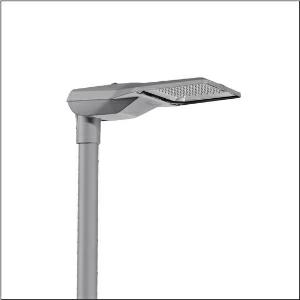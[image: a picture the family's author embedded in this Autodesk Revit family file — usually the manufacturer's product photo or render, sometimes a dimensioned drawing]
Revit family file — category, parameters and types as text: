
# Revit family: streetlight_sl_21_midi___st1_0a_5xe3d33s08nb_54c0
name_source: partatom
category: Lighting Fixtures
units: mm (PartAtom-declared; Revit-internal decimal feet)

## family parameters
Cut with Voids When Loaded = No
Host = Face
Light Source = No
Part Type = Normal
Room Calculation Point = No
Round Connector Dimension = Use Diameter
Shared = No

## types (1)
- --- (1 x LED, 22700 lm, 151.2 W, 3000K)
    Apparent Load = 151 VA
    CIE Flux Codes = 40 73 97 100 100
    Color Rendering = 70
    Color Temperature = 3000K
    Default Elevation = 1800 mm
    Description = Streetlight SL 21 midi, mast luminaire, primary light control with lens, of PMMA, primary optical cover: cover, of toughened safety glass, transparent, light distribution: ST1.0a, light emission: direct distribution, primary light characteristic: asymmetric, installation type: side-entry, post-top, LED, High Power LED, rated luminous flux: 22.700lm, luminous efficacy: 150lm/W, light colour: 730, colour temperature: 3000K, control: flexible luminous flux parameterisation, time-dependent luminous flux control, constant luminous flux control, overheat protection, presetting dimming logarithmic, mains connection: 230..240V, AC, 50/60Hz, start of lifetime: 151W, end of service life: 157W, reduction: 70W, luminaire housing, of diecast aluminium, powder-coated, Siteco® metallic grey (DB 702S), corrosivity category C5 mid according to DIN EN ISO 12944, please order mast flange separately, inclination adjustable: 0°, 5°, 10°, 15°, sealing non-destructively replaceable, multi-level sealing system, length: 644mm, width: 335mm, height: 110mm, mast flange for spigot size: 42mm (side-entry): 5XC10008XM4, 60/48mm (side-entry/post-top): 5XC10108XM2, 76/60mm (side-entry/post-top): 5XC10108XM1, Smart Interface above, protection rating (complete): IP66, insulation class (complete): insulation class II (safety insulation), certification: CE, ENEC, ENEC+, VDE, impact resistance: IK09, permissible operating ambient temperature for outdoor applications: -40..+50°C, standard-compliant lighting for roads and squares, packaging unit: 1 piece

Light Distribution: ST1.0a
    Height = 111 mm
    Lamp = 1 x LED
    Lamp Light Flux = 22700 lm
    Lamp Power = 151.2 W
    Lamp count = 1
    Length = 644 mm
    Luminous efficacy = 150 lm/W
    Manufacturer = Siteco
    ModVariant = No
    Model = 5XE3D33S08NB
    Number of Poles = 1
    OnlyDefault = Yes
    Power Factor = 1
    Product Name = Streetlight SL 21 midi | ST1.0a
    Product group = mast luminaire | pylon top
    ProductGroupID = 6100
    Protection Class = Protection class II
    Protection Degree = IP 66
    RLX_Detail_Level = 1
    RLX_Emergency_Light_Flux = 0 lm
    RLX_Emergency_Type = 0
    RLX_Emergency_Type_DB = No
    RlxData = <blob elided: 91497 chars, md5=c86d76ee>
    Socket = socket
    Standby Power = 0 W
    System Light Flux = 22700 lm
    System Power = 151 W
    Type Comments = factory setting: luminous flux: 100 % | dim-lin: 254 | 802 mA
    Type Image = l_1004302.jpg
    URL = http://relux.com
    VarID = @adj_121199
    Voltage = 0 V
    Weight = 0.00 kg
    Width = 336 mm

## geometry (parser evidence)
native form markers: Blend x4, Sweep x11
no freeform markers — native parametric forms only
